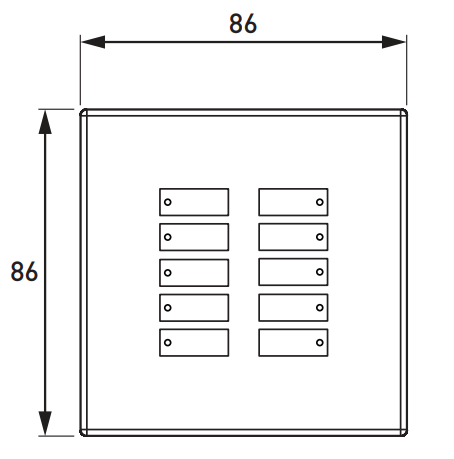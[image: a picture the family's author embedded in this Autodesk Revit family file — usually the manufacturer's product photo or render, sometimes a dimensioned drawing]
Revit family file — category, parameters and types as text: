
# Revit family: Enocean Panel _183X
name_source: partatom
category: Electrical Fixtures
revit_build: Autodesk Revit 2018 (Build: 20170223_1515(x64)
units: mm (PartAtom-declared; Revit-internal decimal feet)

## family parameters
Always vertical = Yes
Cut with Voids When Loaded = No
Maintain Annotation Orientation = No
Part Type = Normal
Room Calculation Point = No
Round Connector Dimension = Use Diameter
Shared = No
Work Plane-Based = Yes

## types (1)
- Single Rocker Switch_Black/White
    Ambient temperature = 0 °C to +50 °C
    Connections = No wiring (power or communications) is required.
    Default Elevation = 0 mm  [stored 0 ft]
    Dimensions = 86 mm × 86 mm × 15 mm
    Environment = Complies with WEEE and RoHS directives
    Frame = Plastic (183 & 184)
    IP code = IP30
    Manufacturer = Helvar
    Material: = Switch rockers: plastic
    Max. No. of switch panels per gateway = 20
    Model = 183 W/183 B
    Mounting = Mount to back box, or mount on glass or flat surface
    Operating frequency = 868 MHz ISM band (Europe)
    Power = Signal power is generated by pressing the EnOcean button
    RED 2014/53/EU = EN 301489-3 EN 300220-2
    Range: = 30 m (unobstructed space)
    Relative humidity = Max. 90 %, noncondensing
    Safety = EN 60950-1
    Storage temperature = –10 °C to +70 °C
    Switch colour = 18xW: white 18xB: black
    Weight = 150 g
    Wireless protocol = ISO/IEC 14543–3–10

note: [stored X ft] marks values corroborated as IEEE doubles in the binary element streams (Revit-internal decimal feet)

## geometry (parser evidence)
native form markers: Sweep x10
no freeform markers — native parametric forms only
